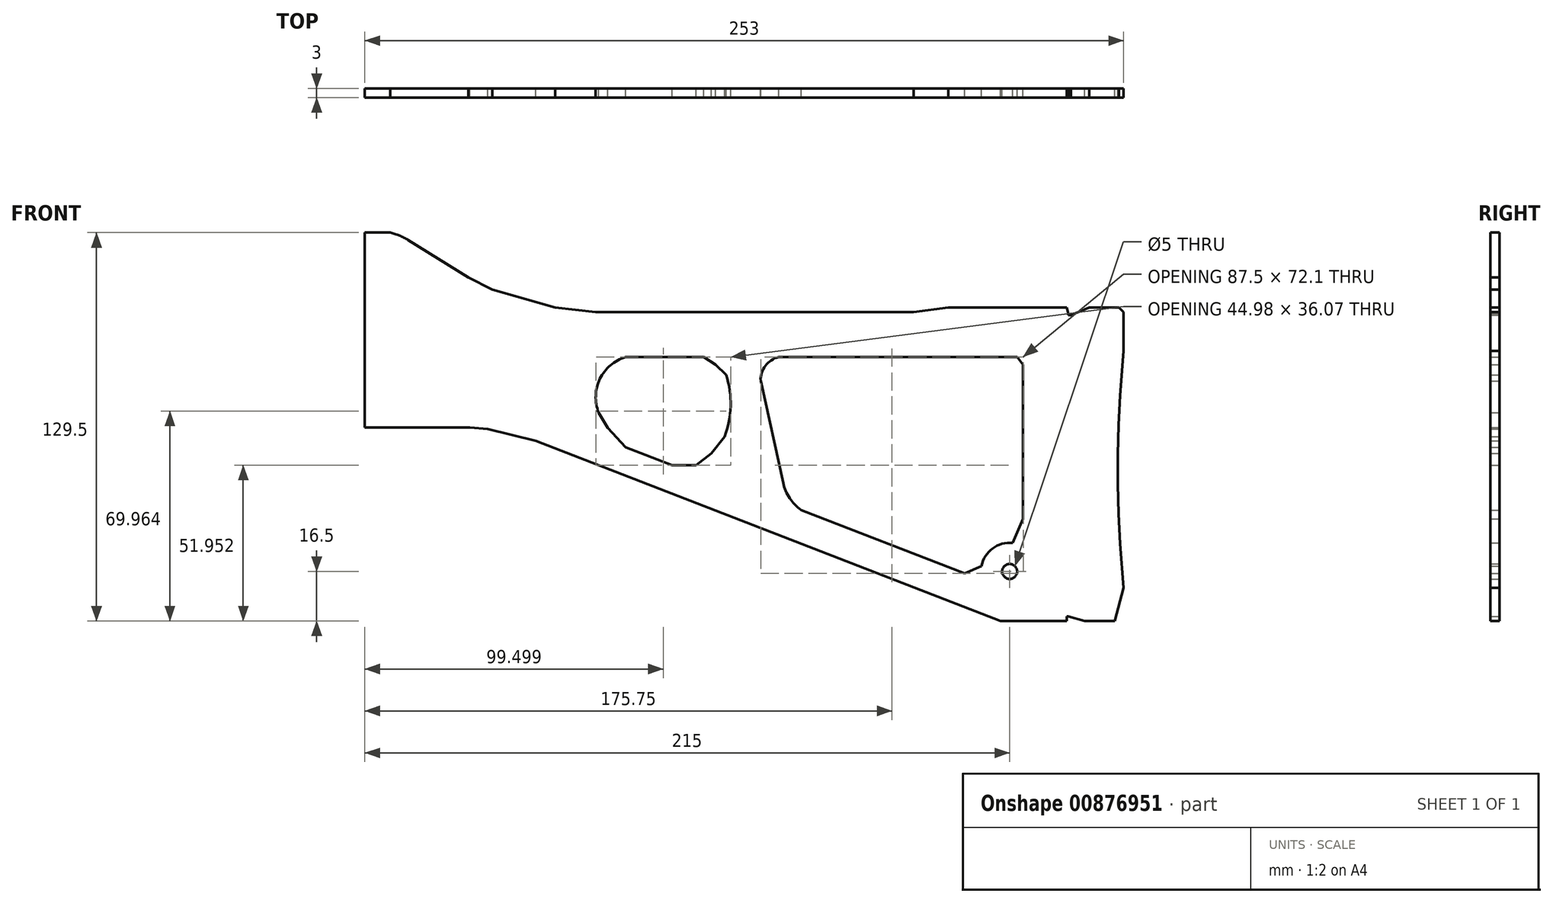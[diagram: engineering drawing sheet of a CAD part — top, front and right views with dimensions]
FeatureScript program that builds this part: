
annotation { "Feature Type Name" : "Feature", "Feature Type Description" : "" }
export const myFeature = defineFeature(function(context is Context, id is Id, definition is map)
    precondition{}
    {
        {
            var Q0;
            Q0=qCreatedBy(makeId("Front.planeOp"),FACE);
            var sketch = newSketch(context, id + "F0", { "sketchPlane" : qUnion([Q0])});
            skLineSegment(sketch, "E0", {"start": v(0, 0) * mm, "end": v(8.5, 0) * mm});
            skLineSegment(sketch, "E1", {"start": v(14.5, -2.5) * mm, "end": v(34.5, -15) * mm});
            skLineSegment(sketch, "E2", {"start": v(34.5, -15) * mm, "end": v(42.5, -19) * mm});
            skLineSegment(sketch, "E3", {"start": v(42.5, -19) * mm, "end": v(63.5, -25) * mm});
            skLineSegment(sketch, "E4", {"start": v(63.5, -25) * mm, "end": v(77, -26.5) * mm});
            skLineSegment(sketch, "E5", {"start": v(77, -26.5) * mm, "end": v(183, -26.5) * mm});
            skLineSegment(sketch, "E6", {"start": v(183, -26.5) * mm, "end": v(194.5, -25) * mm});
            skLineSegment(sketch, "E7", {"start": v(194.5, -25) * mm, "end": v(234, -25) * mm});
            skLineSegment(sketch, "E8", {"start": v(234, -25) * mm, "end": v(234.5, -27) * mm});
            skLineSegment(sketch, "E9", {"start": v(234.5, -27) * mm, "end": v(234.5, -27.5) * mm});
            skLineSegment(sketch, "E10", {"start": v(234.5, -27.5) * mm, "end": v(235.5, -27.5) * mm});
            skLineSegment(sketch, "E11", {"start": v(235.5, -27.5) * mm, "end": v(241.5, -25) * mm});
            skLineSegment(sketch, "E12", {"start": v(241.5, -25) * mm, "end": v(251.5, -25) * mm});
            skLineSegment(sketch, "E13", {"start": v(251.5, -25) * mm, "end": v(253, -26.5) * mm});
            skLineSegment(sketch, "E14", {"start": v(253, -26.5) * mm, "end": v(253, -39.5) * mm});
            skLineSegment(sketch, "E15", {"start": v(253, -118.5) * mm, "end": v(250, -129.5) * mm});
            skLineSegment(sketch, "E16", {"start": v(250, -129.5) * mm, "end": v(240, -129.5) * mm});
            skLineSegment(sketch, "E17", {"start": v(240, -129.5) * mm, "end": v(234.5, -128) * mm});
            skLineSegment(sketch, "E18", {"start": v(234.5, -128) * mm, "end": v(234, -128) * mm});
            skLineSegment(sketch, "E19", {"start": v(234, -128) * mm, "end": v(234, -129.5) * mm});
            skLineSegment(sketch, "E20", {"start": v(234, -129.5) * mm, "end": v(212, -129.5) * mm});
            skLineSegment(sketch, "E21", {"start": v(212, -129.5) * mm, "end": v(57, -69.5) * mm});
            skLineSegment(sketch, "E22", {"start": v(57, -69.5) * mm, "end": v(41, -65.5) * mm});
            skLineSegment(sketch, "E23", {"start": v(41, -65.5) * mm, "end": v(35, -65) * mm});
            skLineSegment(sketch, "E24", {"start": v(35, -65) * mm, "end": v(0, -65) * mm});
            skLineSegment(sketch, "E25", {"start": v(0, -65) * mm, "end": v(0, 0) * mm});
            skLineSegment(sketch, "E26", {"start": v(87, -41.5) * mm, "end": v(113, -41.5) * mm});
            skLineSegment(sketch, "E27", {"start": v(87, -71.57) * mm, "end": v(102.5, -77.57) * mm});
            skLineSegment(sketch, "E28", {"start": v(138, -41.5) * mm, "end": v(217.5, -41.5) * mm});
            skLineSegment(sketch, "E29", {"start": v(217.5, -41.5) * mm, "end": v(219.5, -44) * mm});
            skLineSegment(sketch, "E30", {"start": v(219.5, -44) * mm, "end": v(219.5, -95.5) * mm});
            skLineSegment(sketch, "E31", {"start": v(219.5, -95.5) * mm, "end": v(216, -103.5) * mm});
            skLineSegment(sketch, "E32", {"start": v(145.5, -92.5) * mm, "end": v(200, -113.6) * mm});
            skLineSegment(sketch, "E33", {"start": v(200, -113.6) * mm, "end": v(205.62, -111.18) * mm});
            skLineSegment(sketch, "E34", {"start": v(132, -49.5) * mm, "end": v(139.5, -83.5) * mm});
            skPoint(sketch, "E35", {"position": v(77, -41.5) * mm});
            skLineSegment(sketch, "E36", {"start": v(113, -41.5) * mm, "end": v(117, -44) * mm});
            skLineSegment(sketch, "E37", {"start": v(117, -44) * mm, "end": v(120.5, -47.5) * mm});
            skLineSegment(sketch, "E38", {"start": v(87, -71.57) * mm, "end": v(81, -65.07) * mm});
            skLineSegment(sketch, "E39", {"start": v(81, -65.07) * mm, "end": v(78, -60.07) * mm});
            skPoint(sketch, "E40", {"position": v(77, -55) * mm});
            skArc(sketch, "E41", {"start": v(87, -41.5) * mm, "mid": v(78.4, -48.8) * mm, "end": v(78, -60.07) * mm});
            skLineSegment(sketch, "E42", {"start": v(102.5, -77.57) * mm, "end": v(110.5, -77.57) * mm});
            skLineSegment(sketch, "E43", {"start": v(110.5, -77.57) * mm, "end": v(115.5, -73.57) * mm});
            skLineSegment(sketch, "E44", {"start": v(115.5, -73.57) * mm, "end": v(120, -68.07) * mm});
            skPoint(sketch, "E45", {"position": v(122, -57) * mm});
            skArc(sketch, "E46", {"start": v(120, -68.07) * mm, "mid": v(122, -57.83) * mm, "end": v(120.5, -47.5) * mm});
            skPoint(sketch, "E47", {"position": v(215, -113) * mm});
            skArc(sketch, "E48", {"start": v(216, -103.5) * mm, "mid": v(209.32, -105.32) * mm, "end": v(205.62, -111.18) * mm});
            skCircle(sketch, "E49", {"center": v(215, -113) * mm, "radius": 2.5 * mm});
            skPoint(sketch, "E50", {"position": v(133.5, -44.5) * mm});
            skArc(sketch, "E51", {"start": v(138, -41.5) * mm, "mid": v(133.56, -44.42) * mm, "end": v(132, -49.5) * mm});
            skArc(sketch, "E52", {"start": v(139.5, -83.5) * mm, "mid": v(141.66, -88.56) * mm, "end": v(145.5, -92.5) * mm});
            skArc(sketch, "E53", {"start": v(14.5, -2.5) * mm, "mid": v(11.6, -1) * mm, "end": v(8.5, 0) * mm});
            skArc(sketch, "E54", {"start": v(253, -39.5) * mm, "mid": v(251.05, -79) * mm, "end": v(253, -118.5) * mm});
            skPoint(sketch, "E55", {"position": v(253, -79) * mm});
            skSolve(sketch);
        }
        {
            var Q0;
            Q0=makeQuery(id+"F0.imprint","IMPRINT",FACE,{"disambiguationData":[TD([[makeQuery(id+"F0.imprint","IMPRINT",EDGE,{"derivedFrom":sQuery(id+"F0.wireOp",EDGE,"E0")}),-1.0]])]});
            extrude(context, id + "F1", {"entities" : qUnion([Q0]), "depth" : 3 * mm, "offsetDistance" : 25 * mm});
        }
    });
